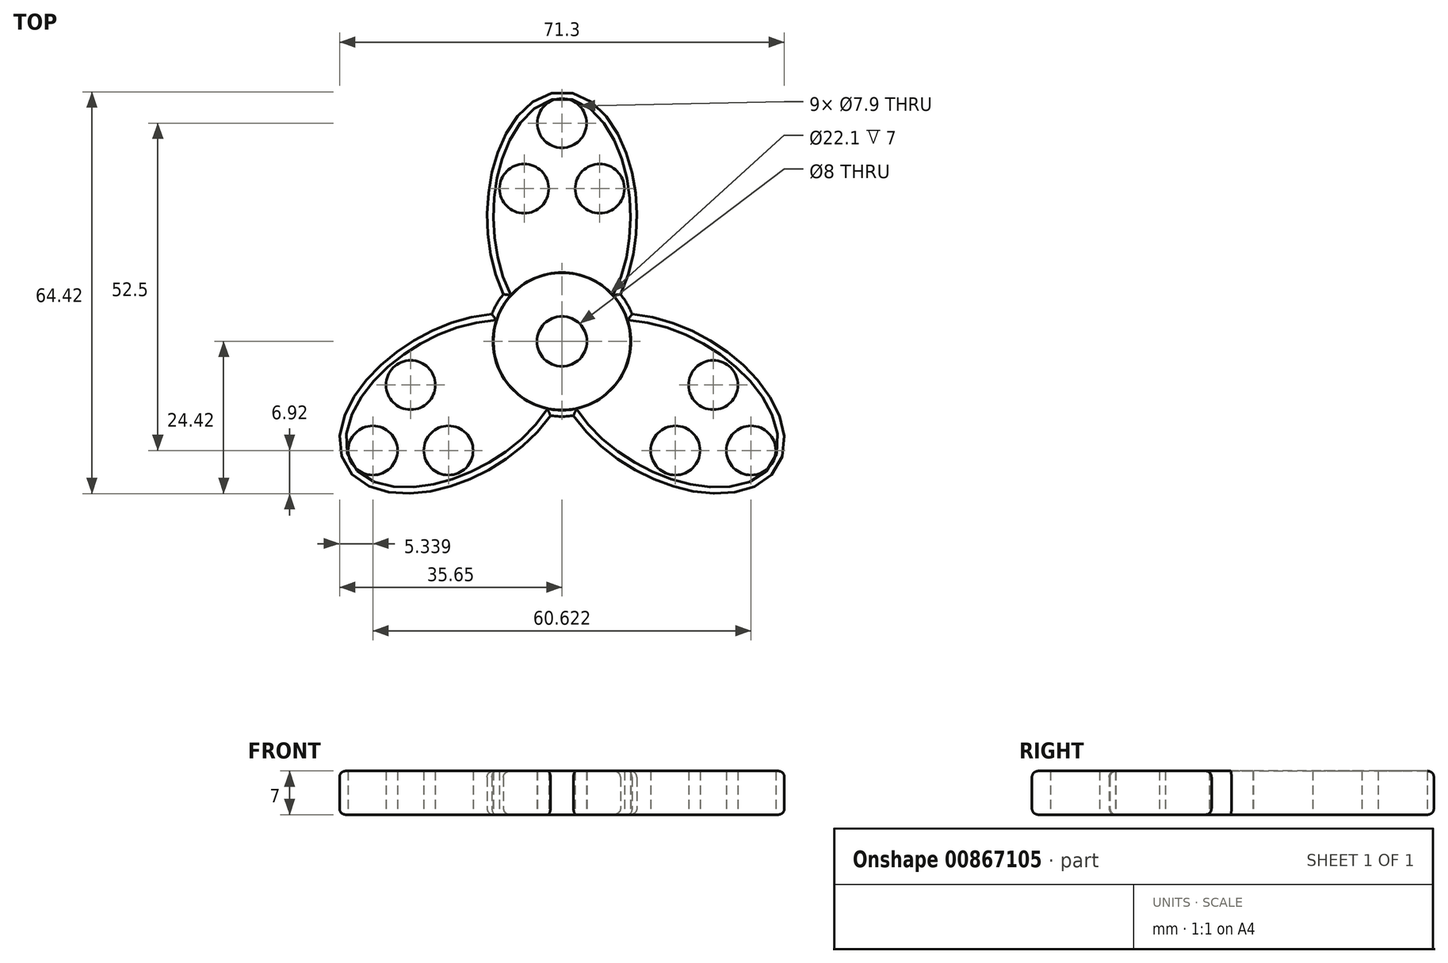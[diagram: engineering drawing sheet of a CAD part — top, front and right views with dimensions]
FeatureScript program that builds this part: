
annotation { "Feature Type Name" : "Feature", "Feature Type Description" : "" }
export const myFeature = defineFeature(function(context is Context, id is Id, definition is map)
    precondition{}
    {
        {
            var Q0;
            Q0=qCreatedBy(makeId("Top.planeOp"),FACE);
            var sketch = newSketch(context, id + "F0", { "sketchPlane" : qUnion([Q0])});
            skCircle(sketch, "E0", {"center": v(0, 0) * mm, "radius": 11 * mm});
            skCircle(sketch, "E1", {"center": v(0, 0) * mm, "radius": 4 * mm});
            skSolve(sketch);
        }
        {
            var Q0;
            Q0 = qSketchRegion(id + "F0", true);
            extrude(context, id + "F1", {"entities" : qUnion([Q0]), "depth" : 7 * mm, "offsetDistance" : 25 * mm});
        }
        {
            var Q0;
            Q0=qCreatedBy(makeId("Top.planeOp"),FACE);
            var sketch = newSketch(context, id + "F2", { "sketchPlane" : qUnion([Q0])});
            skCircle(sketch, "E2", {"center": v(0, 0) * mm, "radius": 40 * mm, "construction": true});
            skCircle(sketch, "E3", {"center": v(0, 28) * mm, "radius": 12 * mm, "construction": true});
            skCircle(sketch, "E4.0", {"center": v(0, 28) * mm, "radius": 7 * mm, "construction": true});
            skCircle(sketch, "E5", {"center": v(0, 35) * mm, "radius": 3.95 * mm});
            skCircle(sketch, "E6.1.0", {"center": v(-6.06, 24.5) * mm, "radius": 3.95 * mm});
            skCircle(sketch, "E6.2.0", {"center": v(6.06, 24.5) * mm, "radius": 3.95 * mm});
            skLineSegment(sketch, "E7", {"start": v(0, 0) * mm, "end": v(0, 40) * mm, "construction": true});
            skEllipticalArc(sketch, "E8", {});
            skCircle(sketch, "E9.1.0", {"center": v(-24.25, -14) * mm, "radius": 12 * mm, "construction": true});
            skEllipticalArc(sketch, "E9.1.1", {});
            skCircle(sketch, "E9.1.2", {"center": v(-30.31, -17.5) * mm, "radius": 3.95 * mm});
            skLineSegment(sketch, "E9.1.3", {"start": v(0, 0) * mm, "end": v(-34.64, -20) * mm, "construction": true});
            skCircle(sketch, "E9.1.4", {"center": v(-24.25, -7) * mm, "radius": 3.95 * mm});
            skCircle(sketch, "E9.1.5", {"center": v(-24.25, -14) * mm, "radius": 7 * mm, "construction": true});
            skCircle(sketch, "E9.1.6", {"center": v(-18.19, -17.5) * mm, "radius": 3.95 * mm});
            skCircle(sketch, "E9.2.0", {"center": v(24.25, -14) * mm, "radius": 12 * mm, "construction": true});
            skEllipticalArc(sketch, "E9.2.1", {});
            skCircle(sketch, "E9.2.2", {"center": v(30.31, -17.5) * mm, "radius": 3.95 * mm});
            skLineSegment(sketch, "E9.2.3", {"start": v(0, 0) * mm, "end": v(34.64, -20) * mm, "construction": true});
            skCircle(sketch, "E9.2.4", {"center": v(18.19, -17.5) * mm, "radius": 3.95 * mm});
            skCircle(sketch, "E9.2.5", {"center": v(24.25, -14) * mm, "radius": 7 * mm, "construction": true});
            skCircle(sketch, "E9.2.6", {"center": v(24.25, -7) * mm, "radius": 3.95 * mm});
            skCircle(sketch, "E10", {"center": v(0, 0) * mm, "radius": 11.05 * mm});
            skArc(sketch, "E11.0", {"start": v(-1.84, -11.9) * mm, "mid": v(0, -12.05) * mm, "end": v(1.84, -11.9) * mm});
            skPoint(sketch, "E12.orphan", {"position": v(-10.13, 4.42) * mm});
            skPoint(sketch, "E13.orphan", {"position": v(-1.24, -10.98) * mm});
            skArc(sketch, "E14.trimOffspring", {"start": v(11.23, 4.36) * mm, "mid": v(10.44, 6.03) * mm, "end": v(9.4, 7.55) * mm});
            skPoint(sketch, "E15.orphan", {"position": v(1.24, -10.98) * mm});
            skPoint(sketch, "E16.orphan", {"position": v(10.13, 4.42) * mm});
            skPoint(sketch, "E17.orphan", {"position": v(8.89, 6.56) * mm});
            skArc(sketch, "E18.trimOffspring", {"start": v(-9.4, 7.55) * mm, "mid": v(-10.44, 6.03) * mm, "end": v(-11.23, 4.36) * mm});
            skPoint(sketch, "E19.orphan", {"position": v(-8.89, 6.56) * mm});
            const initialGuessF2  = {"E8": [0, 0.02, 0, 1, 0.02, 0.012, 4.040458310034012, 2.2427269971455743], "E9.1.1": [-0.017320508075688773, -0.01, -0.8660254037844388, -0.5, 0.02, 0.012, 4.040458310034012, 2.2427269971455743], "E9.2.1": [0.01732050807568877, -0.01, 0.8660254037844384, -0.5, 0.02, 0.012, 4.040458310034012, 2.2427269971455743]};
            skSetInitialGuess(sketch, initialGuessF2);
            skSolve(sketch);
        }
        {
            var Q0;
            Q0 = qSketchRegion(id + "F2", true);
            extrude(context, id + "F3", {"entities" : qUnion([Q0]), "operationType" : NewBodyOperationType.ADD, "depth" : 7 * mm, "offsetDistance" : 25 * mm});
        }
        {
            var Q0;
            Q0=makeQuery(id+"F3.opExtrude","CAP_EDGE",EDGE,{"disambiguationData":[OSD([sQuery(id+"F2.wireOp",EDGE,"E8")])],"isStart":false});
            var Q1;
            Q1=makeQuery(id+"F3.opExtrude","CAP_EDGE",EDGE,{"disambiguationData":[OSD([sQuery(id+"F2.wireOp",EDGE,"E9.2.1")])],"isStart":false});
            var Q2;
            Q2=makeQuery(id+"F3.opExtrude","CAP_EDGE",EDGE,{"disambiguationData":[OSD([sQuery(id+"F2.wireOp",EDGE,"E9.1.1")])],"isStart":false});
            var Q3;
            Q3=makeQuery(id+"F3.opExtrude","CAP_EDGE",EDGE,{"disambiguationData":[OSD([sQuery(id+"F2.wireOp",EDGE,"E18.trimOffspring")])],"isStart":false});
            var Q4;
            Q4=makeQuery(id+"F3.opExtrude","CAP_EDGE",EDGE,{"disambiguationData":[OSD([sQuery(id+"F2.wireOp",EDGE,"E14.trimOffspring")])],"isStart":false});
            var Q5;
            Q5=makeQuery(id+"F3.opExtrude","CAP_EDGE",EDGE,{"disambiguationData":[OSD([sQuery(id+"F2.wireOp",EDGE,"E11.0")])],"isStart":false});
            var Q6;
            Q6=makeQuery(id+"F3.opExtrude","CAP_EDGE",EDGE,{"disambiguationData":[OSD([sQuery(id+"F2.wireOp",EDGE,"E8")])],"isStart":true});
            var Q7;
            Q7=makeQuery(id+"F3.opExtrude","CAP_EDGE",EDGE,{"disambiguationData":[OSD([sQuery(id+"F2.wireOp",EDGE,"E9.1.1")])],"isStart":true});
            var Q8;
            Q8=makeQuery(id+"F3.opExtrude","CAP_EDGE",EDGE,{"disambiguationData":[OSD([sQuery(id+"F2.wireOp",EDGE,"E9.2.1")])],"isStart":true});
            var Q9;
            Q9=makeQuery(id+"F3.opExtrude","CAP_EDGE",EDGE,{"disambiguationData":[OSD([sQuery(id+"F2.wireOp",EDGE,"E14.trimOffspring")])],"isStart":true});
            var Q10;
            Q10=makeQuery(id+"F3.opExtrude","CAP_EDGE",EDGE,{"disambiguationData":[OSD([sQuery(id+"F2.wireOp",EDGE,"E18.trimOffspring")])],"isStart":true});
            var Q11;
            Q11=makeQuery(id+"F3.opExtrude","CAP_EDGE",EDGE,{"disambiguationData":[OSD([sQuery(id+"F2.wireOp",EDGE,"E11.0")])],"isStart":true});
            fillet(context, id + "F4", {"entities" : qUnion([Q0, Q1, Q2, Q3, Q4, Q5, Q6, Q7, Q8, Q9, Q10, Q11]), "radius" : 1 * mm, "tangentPropagation" : true, "allowEdgeOverflow" : false});
        }
    });
